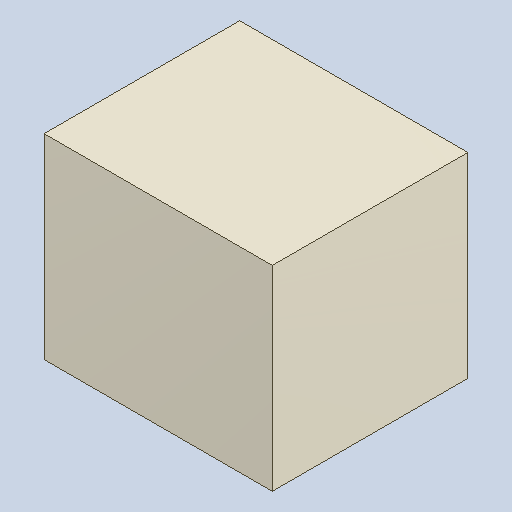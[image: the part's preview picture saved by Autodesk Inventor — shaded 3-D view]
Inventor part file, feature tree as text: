
AUTODESK INVENTOR PART (.ipt)
format: ipt  version: 2023.4 (Build 274418000, 418)  size: 82,432 bytes
history: native  units: mm
features: extrude x1
ambient origin geometry x8: Origin, YZ Plane, XZ Plane, XY Plane, X Axis, Y Axis, Z Axis, Center Point
bodies: Solid1 (feature_tree)
feature tree (1):
  extrude  "Extruded_10"  [1 undecoded]
note: 1 required parameter value undecoded (feature->parameter linkage not recoverable at this tier; creation-order binding heuristic only, values carry confidence <= 0.55)
